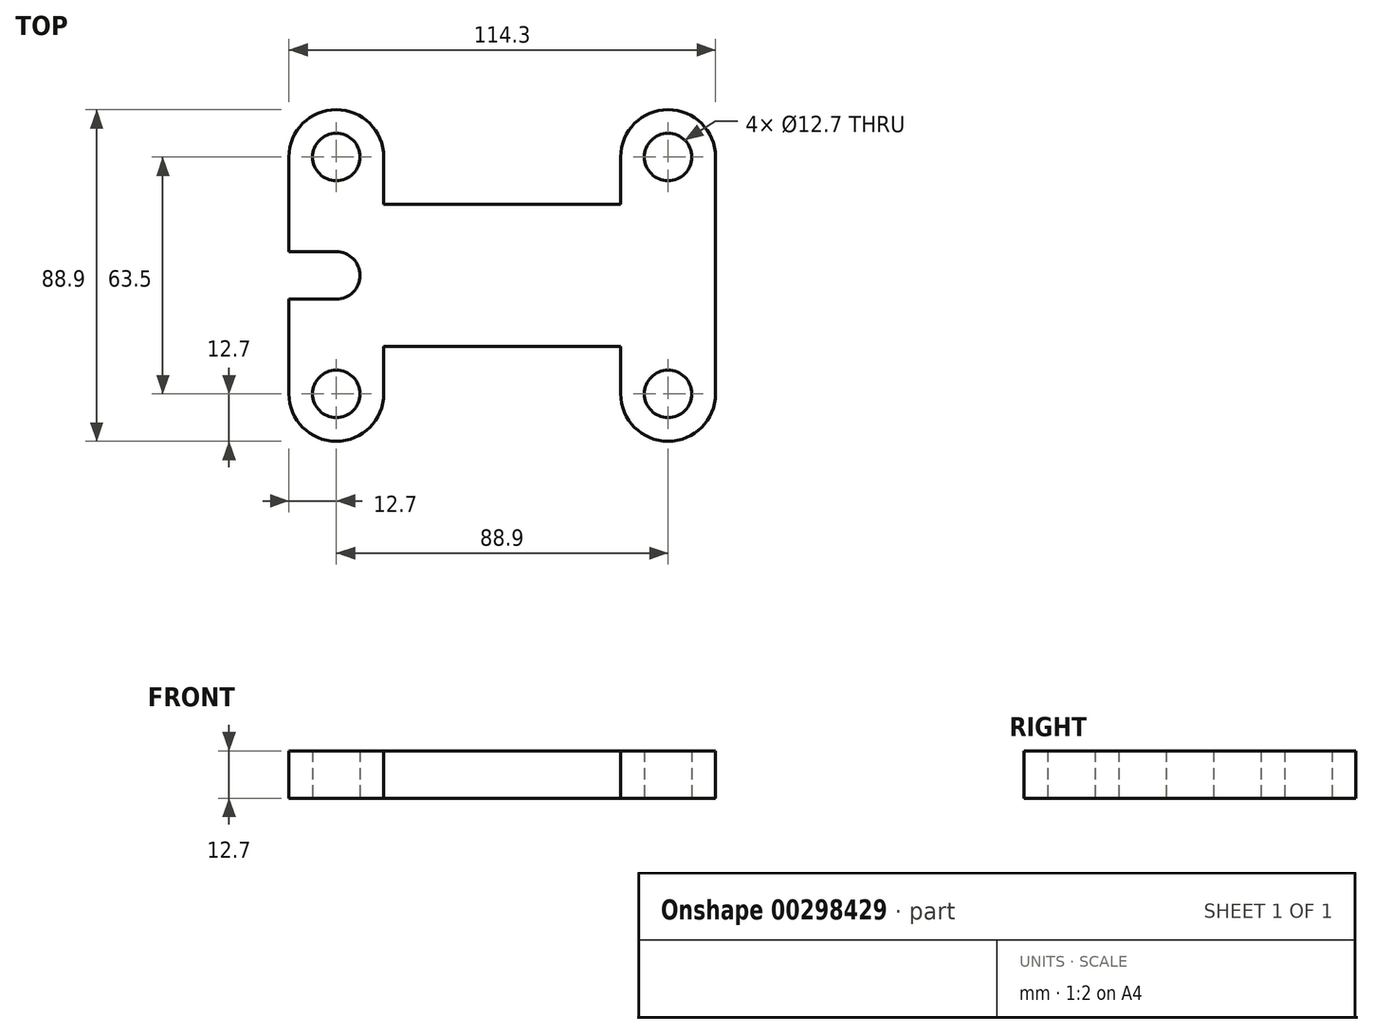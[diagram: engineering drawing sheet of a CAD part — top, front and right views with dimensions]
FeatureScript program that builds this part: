
annotation { "Feature Type Name" : "Feature", "Feature Type Description" : "" }
export const myFeature = defineFeature(function(context is Context, id is Id, definition is map)
    precondition{}
    {
        {
            var Q0;
            Q0=qCreatedBy(makeId("Top.planeOp"),FACE);
            var sketch = newSketch(context, id + "F0", { "sketchPlane" : qUnion([Q0])});
            skCircle(sketch, "E0", {"center": v(88.9, 63.5) * mm, "radius": 6.35 * mm});
            skCircle(sketch, "E1", {"center": v(88.9, 0) * mm, "radius": 6.35 * mm});
            skCircle(sketch, "E2", {"center": v(0, 0) * mm, "radius": 6.35 * mm});
            skCircle(sketch, "E3", {"center": v(0, 63.5) * mm, "radius": 6.35 * mm});
            skArc(sketch, "E4", {"start": v(88.9, -12.7) * mm, "mid": v(79.92, -8.98) * mm, "end": v(76.2, 0) * mm});
            skArc(sketch, "E5", {"start": v(88.9, -12.7) * mm, "mid": v(97.88, -8.98) * mm, "end": v(101.6, 0) * mm});
            skArc(sketch, "E6", {"start": v(88.9, 76.2) * mm, "mid": v(79.92, 72.48) * mm, "end": v(76.2, 63.5) * mm});
            skArc(sketch, "E7", {"start": v(88.9, 76.2) * mm, "mid": v(97.88, 72.48) * mm, "end": v(101.6, 63.5) * mm});
            skArc(sketch, "E8", {"start": v(0, -12.7) * mm, "mid": v(8.98, -8.98) * mm, "end": v(12.7, 0) * mm});
            skArc(sketch, "E9", {"start": v(0, -12.7) * mm, "mid": v(-8.98, -8.98) * mm, "end": v(-12.7, 0) * mm});
            skArc(sketch, "E10", {"start": v(0, 76.2) * mm, "mid": v(8.98, 72.48) * mm, "end": v(12.7, 63.5) * mm});
            skArc(sketch, "E11", {"start": v(0, 76.2) * mm, "mid": v(-8.98, 72.48) * mm, "end": v(-12.7, 63.5) * mm});
            skLineSegment(sketch, "E12", {"start": v(101.6, 63.5) * mm, "end": v(101.6, 50.8) * mm});
            skLineSegment(sketch, "E13", {"start": v(76.2, 50.8) * mm, "end": v(76.2, 63.5) * mm});
            skLineSegment(sketch, "E14", {"start": v(12.7, 63.5) * mm, "end": v(12.7, 50.8) * mm});
            skLineSegment(sketch, "E15", {"start": v(-12.7, 50.8) * mm, "end": v(-12.7, 63.5) * mm});
            skLineSegment(sketch, "E16", {"start": v(-12.7, 0) * mm, "end": v(-12.7, 12.7) * mm});
            skLineSegment(sketch, "E17", {"start": v(12.7, 12.7) * mm, "end": v(12.7, 0) * mm});
            skLineSegment(sketch, "E18", {"start": v(76.2, 0) * mm, "end": v(76.2, 12.7) * mm});
            skLineSegment(sketch, "E19", {"start": v(101.6, 12.7) * mm, "end": v(101.6, 0) * mm});
            skLineSegment(sketch, "E20.bottom", {"start": v(12.7, 50.8) * mm, "end": v(76.2, 50.8) * mm});
            skLineSegment(sketch, "E20.top", {"start": v(12.7, 12.7) * mm, "end": v(76.2, 12.7) * mm});
            skLineSegment(sketch, "E20.left", {"start": v(-12.7, 50.8) * mm, "end": v(-12.7, 38.1) * mm});
            skLineSegment(sketch, "E20.right", {"start": v(101.6, 50.8) * mm, "end": v(101.6, 12.7) * mm});
            skPoint(sketch, "E21", {"position": v(0, 31.75) * mm});
            skArc(sketch, "E22", {"start": v(6.35, 31.75) * mm, "mid": v(4.5, 36.24) * mm, "end": v(0, 38.1) * mm});
            skArc(sketch, "E23", {"start": v(6.35, 31.75) * mm, "mid": v(4.5, 27.26) * mm, "end": v(0, 25.4) * mm});
            skLineSegment(sketch, "E24", {"start": v(0, 38.1) * mm, "end": v(-12.7, 38.1) * mm});
            skLineSegment(sketch, "E25", {"start": v(0, 25.4) * mm, "end": v(-12.7, 25.4) * mm});
            skLineSegment(sketch, "E26.trimOffspring", {"start": v(-12.7, 25.4) * mm, "end": v(-12.7, 12.7) * mm});
            skSolve(sketch);
        }
        {
            var Q0;
            Q0=qSketchRegion(id+"F0",true);
            extrude(context, id + "F1", {"entities" : qUnion([Q0]), "depth" : 12.7 * mm});
        }
    });
